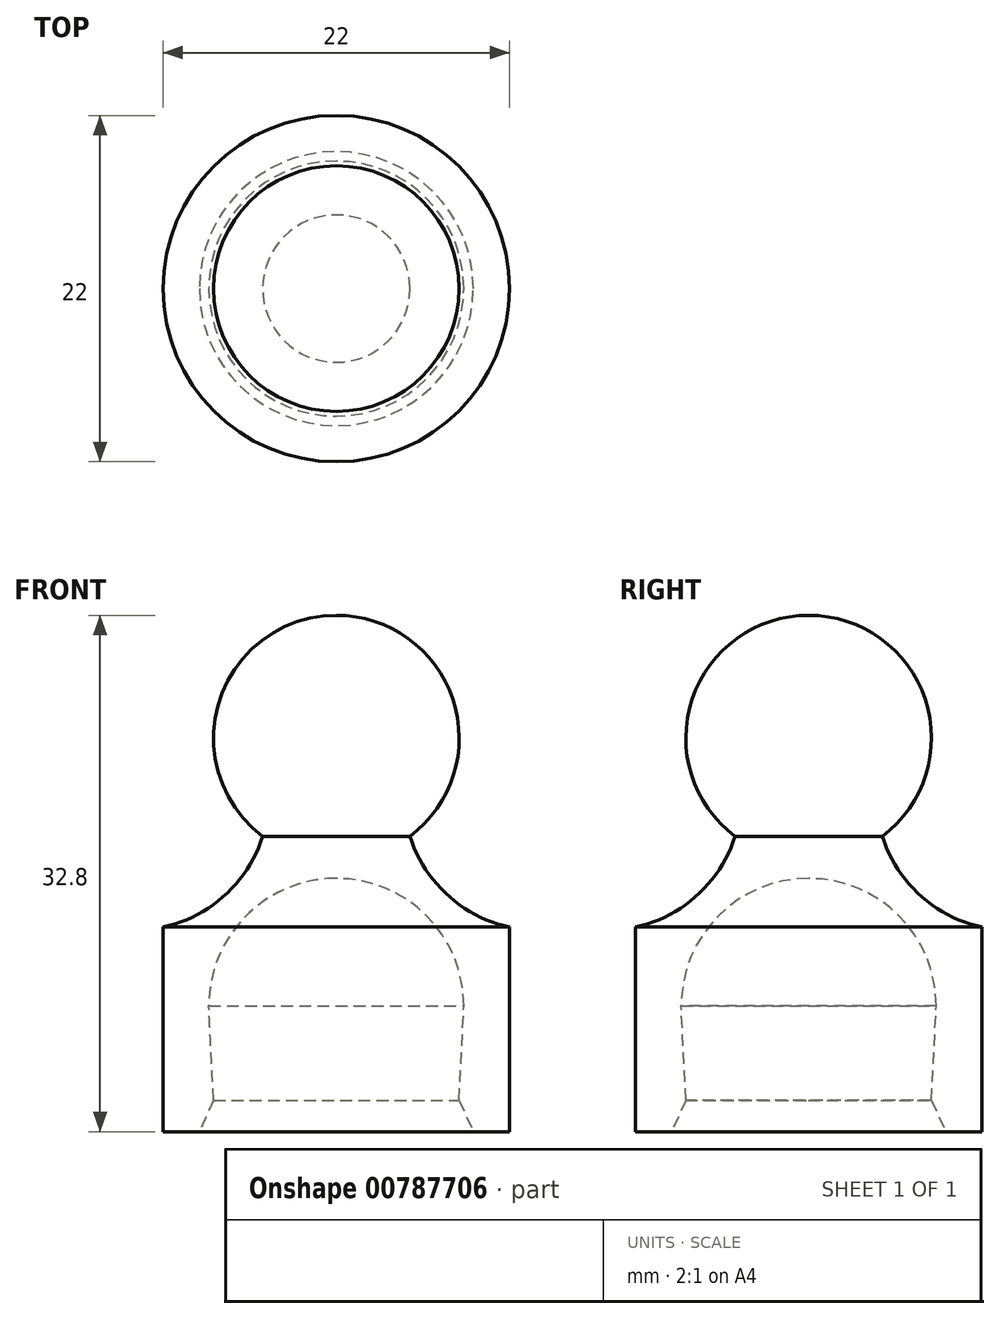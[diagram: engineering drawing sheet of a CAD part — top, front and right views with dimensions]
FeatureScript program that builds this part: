
annotation { "Feature Type Name" : "Feature", "Feature Type Description" : "" }
export const myFeature = defineFeature(function(context is Context, id is Id, definition is map)
    precondition{}
    {
        {
            var Q0;
            Q0=qCreatedBy(makeId("Front.planeOp"),FACE);
            var sketch = newSketch(context, id + "F0", { "sketchPlane" : qUnion([Q0])});
            skLineSegment(sketch, "E0", {"start": v(11, 0) * mm, "end": v(11, 13) * mm});
            skLineSegment(sketch, "E1", {"start": v(-11, 0) * mm, "end": v(-11, 13) * mm});
            skLineSegment(sketch, "E2", {"start": v(-7.7, 0) * mm, "end": v(-8.1, 7.99) * mm});
            skLineSegment(sketch, "E3", {"start": v(7.7, 0) * mm, "end": v(8.1, 7.99) * mm});
            skArc(sketch, "E4", {"start": v(8.1, 7.99) * mm, "mid": v(0, 16.09) * mm, "end": v(-8.1, 7.99) * mm});
            skCircle(sketch, "E5", {"center": v(0, 25) * mm, "radius": 7.8 * mm});
            skLineSegment(sketch, "E6", {"start": v(0, 0) * mm, "end": v(0, 59.18) * mm});
            skLineSegment(sketch, "E7", {"start": v(-11, 0) * mm, "end": v(-7.7, 0) * mm});
            skPoint(sketch, "E8", {"position": v(-4.68, 18.76) * mm});
            skPoint(sketch, "E9", {"position": v(-11, 13) * mm});
            skArc(sketch, "E10", {"start": v(-11, 13) * mm, "mid": v(-7.06, 15.03) * mm, "end": v(-4.68, 18.76) * mm});
            skSolve(sketch);
        }
        {
            var Q0;
            {var subQ0=sQuery(id+"F0.wireOp",EDGE,"E5");var subQ1=makeQuery(id+"F0.imprint","INTERSECT",VERTEX,{"derivedFrom":[subQ0,sQuery(id+"F0.wireOp",EDGE,"oF7ZrrZJ-dgcz-xk90-W0hz-1vPMBmMqkNQW")]});Q0=makeQuery(id+"F0.imprint","IMPRINT",FACE,{"disambiguationData":[TD([[makeQuery(id+"F0.imprint","IMPRINT",EDGE,{"disambiguationData":[TD([[subQ1,1.0]])],"derivedFrom":subQ0}),1.0]])]});}
            var Q1;
            Q1=makeQuery(id+"F0.imprint","IMPRINT",FACE,{"disambiguationData":[TD([[makeQuery(id+"F0.imprint","IMPRINT",EDGE,{"derivedFrom":sQuery(id+"F0.wireOp",EDGE,"E1")}),-1.0]])]});
            var Q2;
            Q2=sQuery(id+"F0.wireOp",EDGE,"E6");
            revolve(context, id + "F1", {"surfaceOperationType" : NewSurfaceOperationType.NEW, "entities" : qUnion([Q0, Q1]), "axis" : qUnion([Q2]), "revolveType" : RevolveType.FULL});
        }
        {
            var Q0;
            Q0=makeQuery(id+"F1.opRevolve","SWEPT_EDGE",EDGE,{"disambiguationData":[OSD([sQuery(id+"F0.wireOp",EDGE,"E2"),sQuery(id+"F0.wireOp",EDGE,"E7")])]});
            chamfer(context, id + "F2", {"entities" : qUnion([Q0]), "chamferType" : ChamferType.TWO_OFFSETS, "width1" : 2 * mm, "oppositeDirection" : false, "width2" : 1 * mm, "tangentPropagation" : true});
        }
    });
